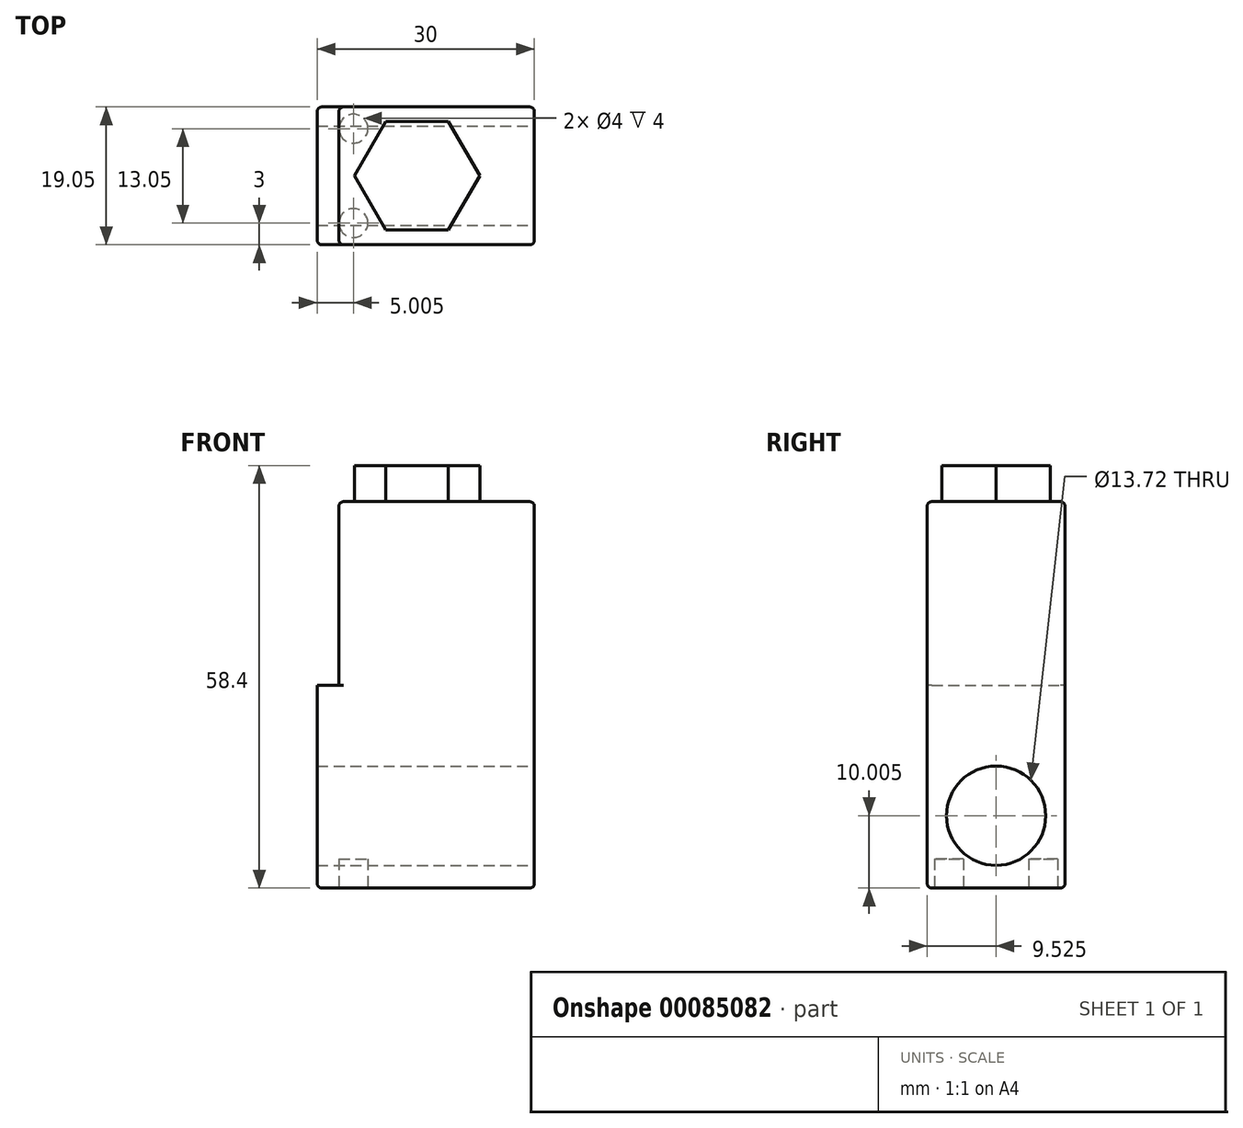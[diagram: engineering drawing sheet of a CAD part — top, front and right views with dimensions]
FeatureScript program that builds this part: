
annotation { "Feature Type Name" : "Feature", "Feature Type Description" : "" }
export const myFeature = defineFeature(function(context is Context, id is Id, definition is map)
    precondition{}
    {
        {
            var Q0;
            Q0=qCreatedBy(makeId("Front.planeOp"),FACE);
            var sketch = newSketch(context, id + "F0", { "sketchPlane" : qUnion([Q0])});
            skLineSegment(sketch, "E0.bottom", {"start": v(-15.44, -0.4) * mm, "end": v(14.56, -0.4) * mm});
            skLineSegment(sketch, "E0.top", {"start": v(-15.44, -28.4) * mm, "end": v(14.56, -28.4) * mm});
            skLineSegment(sketch, "E0.left", {"start": v(-15.44, -0.4) * mm, "end": v(-15.44, -28.4) * mm});
            skLineSegment(sketch, "E0.right", {"start": v(14.56, -0.4) * mm, "end": v(14.56, -28.4) * mm});
            skSolve(sketch);
        }
        {
            var Q0;
            Q0=qSketchRegion(id+"F0",true);
            var Q1;
            Q1=qSketchRegion(id+"F2",true);
            extrude(context, id + "F1", {"entities" : qUnion([Q0, Q1]), "depth" : 19.05 * mm});
        }
        {
            var Q0;
            Q0=makeQuery(id+"F1.opExtrude","SWEPT_FACE",FACE,{"disambiguationData":[OSD([sQuery(id+"F0.wireOp",EDGE,"E0.right")])]});
            var sketch = newSketch(context, id + "F2", { "sketchPlane" : qUnion([Q0])});
            skCircle(sketch, "E1", {"center": v(-9.53, -18.4) * mm, "radius": 6.86 * mm});
            skSolve(sketch);
        }
        {
            var Q0;
            Q0=qSketchRegion(id+"F2",true);
            extrude(context, id + "F3", {"entities" : qUnion([Q0]), "operationType" : NewBodyOperationType.REMOVE, "endBound" : BoundingType.THROUGH_ALL, "oppositeDirection" : true, "depth" : 25.4 * mm});
        }
        {
            var Q0;
            Q0=makeQuery(id+"F1.opExtrude","SWEPT_FACE",FACE,{"disambiguationData":[OSD([sQuery(id+"F0.wireOp",EDGE,"E0.bottom")])]});
            var sketch = newSketch(context, id + "F4", { "sketchPlane" : qUnion([Q0])});
            skLineSegment(sketch, "E2.0.0", {"start": v(13.93, 0) * mm, "end": v(-11.8, 0) * mm});
            skArc(sketch, "E2.0.1", {"start": v(-14.8, 0) * mm, "mid": v(-15.25, -0.19) * mm, "end": v(-15.44, -0.64) * mm});
            skLineSegment(sketch, "E2.0.2", {"start": v(-15.44, -0.64) * mm, "end": v(-15.44, -18.41) * mm});
            skArc(sketch, "E2.0.3", {"start": v(-15.44, -18.41) * mm, "mid": v(-15.25, -18.86) * mm, "end": v(-14.8, -19.05) * mm});
            skLineSegment(sketch, "E2.0.4", {"start": v(-14.8, -19.05) * mm, "end": v(13.93, -19.05) * mm});
            skArc(sketch, "E2.0.5", {"start": v(13.93, -19.05) * mm, "mid": v(14.38, -18.86) * mm, "end": v(14.56, -18.41) * mm});
            skLineSegment(sketch, "E2.0.6", {"start": v(14.56, -18.41) * mm, "end": v(14.56, -0.64) * mm});
            skArc(sketch, "E2.0.7", {"start": v(14.56, -0.64) * mm, "mid": v(14.38, -0.19) * mm, "end": v(13.93, 0) * mm});
            skLineSegment(sketch, "E3.bottom", {"start": v(-12.44, 0) * mm, "end": v(13.93, 0) * mm});
            skLineSegment(sketch, "E3.top", {"start": v(-11.8, -19.05) * mm, "end": v(13.93, -19.05) * mm});
            skLineSegment(sketch, "E3.left", {"start": v(-12.44, -0.64) * mm, "end": v(-12.44, -18.42) * mm});
            skLineSegment(sketch, "E3.right", {"start": v(14.56, -0.64) * mm, "end": v(14.56, -18.41) * mm});
            skPoint(sketch, "E4.newPointB", {"position": v(-14.8, 0) * mm});
            skArc(sketch, "E4.filletArc", {"start": v(-11.8, 0) * mm, "mid": v(-12.25, -0.19) * mm, "end": v(-12.44, -0.64) * mm});
            skPoint(sketch, "E5.visualSharp", {"position": v(-12.44, -19.05) * mm});
            skArc(sketch, "E5.filletArc", {"start": v(-12.44, -18.42) * mm, "mid": v(-12.25, -18.86) * mm, "end": v(-11.8, -19.05) * mm});
            skPoint(sketch, "E6.visualSharp", {"position": v(14.56, -19.05) * mm});
            skPoint(sketch, "E7.visualSharp", {"position": v(14.56, 0) * mm});
            skSolve(sketch);
        }
        {
            var Q0;
            Q0=qSketchRegion(id+"F4",true);
            extrude(context, id + "F5", {"entities" : qUnion([Q0]), "operationType" : NewBodyOperationType.ADD, "depth" : 25.4 * mm});
        }
        {
            var Q0;
            Q0=makeQuery(id+"F1.opExtrude","CAP_EDGE",EDGE,{"disambiguationData":[OSD([sQuery(id+"F0.wireOp",EDGE,"E0.right")])],"isStart":false});
            var Q1;
            Q1=makeQuery(id+"F1.opExtrude","CAP_EDGE",EDGE,{"disambiguationData":[OSD([sQuery(id+"F0.wireOp",EDGE,"E0.left")])],"isStart":false});
            var Q2;
            Q2=makeQuery(id+"F1.opExtrude","CAP_EDGE",EDGE,{"disambiguationData":[OSD([sQuery(id+"F0.wireOp",EDGE,"E0.right")])],"isStart":true});
            var Q3;
            Q3=makeQuery(id+"F1.opExtrude","CAP_EDGE",EDGE,{"disambiguationData":[OSD([sQuery(id+"F0.wireOp",EDGE,"E0.left")])],"isStart":true});
            var Q4;
            Q4=makeQuery(id+"F5.opExtrude","CAP_EDGE",EDGE,{"disambiguationData":[OSD([sQuery(id+"F4.wireOp",EDGE,"E3.bottom")])],"isStart":false});
            var Q5;
            Q5=makeQuery(id+"F5.opExtrude","CAP_EDGE",EDGE,{"disambiguationData":[OSD([sQuery(id+"F4.wireOp",EDGE,"E3.right")])],"isStart":false});
            var Q6;
            Q6=makeQuery(id+"F5.opExtrude","CAP_EDGE",EDGE,{"disambiguationData":[OSD([sQuery(id+"F4.wireOp",EDGE,"E3.top")])],"isStart":false});
            var Q7;
            Q7=makeQuery(id+"F5.opExtrude","CAP_EDGE",EDGE,{"disambiguationData":[OSD([sQuery(id+"F4.wireOp",EDGE,"E3.left")])],"isStart":false});
            var Q8;
            Q8=makeQuery(id+"F1.opExtrude","CAP_EDGE",EDGE,{"disambiguationData":[OSD([sQuery(id+"F0.wireOp",EDGE,"E0.top")])],"isStart":true});
            var Q9;
            Q9=makeQuery(id+"F1.opExtrude","SWEPT_EDGE",EDGE,{"disambiguationData":[OSD([sQuery(id+"F0.wireOp",EDGE,"E0.top"),sQuery(id+"F0.wireOp",EDGE,"E0.right")])]});
            var Q10;
            Q10=makeQuery(id+"F1.opExtrude","CAP_EDGE",EDGE,{"disambiguationData":[OSD([sQuery(id+"F0.wireOp",EDGE,"E0.top")])],"isStart":false});
            var Q11;
            Q11=makeQuery(id+"F1.opExtrude","SWEPT_EDGE",EDGE,{"disambiguationData":[OSD([sQuery(id+"F0.wireOp",EDGE,"E0.top"),sQuery(id+"F0.wireOp",EDGE,"E0.left")])]});
            fillet(context, id + "F6", {"entities" : qUnion([Q0, Q1, Q2, Q3, Q4, Q5, Q6, Q7, Q8, Q9, Q10, Q11]), "radius" : 0.64 * mm, "tangentPropagation" : true, "allowEdgeOverflow" : false});
        }
        {
            var Q0;
            Q0=makeQuery(id+"F1.opExtrude","SWEPT_FACE",FACE,{"disambiguationData":[OSD([sQuery(id+"F0.wireOp",EDGE,"E0.top")])]});
            var sketch = newSketch(context, id + "F7", { "sketchPlane" : qUnion([Q0])});
            skLineSegment(sketch, "E8.0.0", {"start": v(-14.8, 18.41) * mm, "end": v(-14.8, 0.64) * mm});
            skLineSegment(sketch, "E8.0.1", {"start": v(-14.8, 0.64) * mm, "end": v(13.93, 0.64) * mm});
            skLineSegment(sketch, "E8.0.2", {"start": v(13.93, 0.64) * mm, "end": v(13.93, 18.41) * mm});
            skLineSegment(sketch, "E8.0.3", {"start": v(13.93, 18.41) * mm, "end": v(-14.8, 18.41) * mm});
            skLineSegment(sketch, "E9.0.0", {"start": v(13.93, 18.41) * mm, "end": v(13.93, 19.05) * mm});
            skLineSegment(sketch, "E9.0.1", {"start": v(13.93, 19.05) * mm, "end": v(-14.8, 19.05) * mm});
            skLineSegment(sketch, "E9.0.2", {"start": v(-14.8, 19.05) * mm, "end": v(-14.8, 18.41) * mm});
            skLineSegment(sketch, "E10.0.0", {"start": v(-14.8, 18.41) * mm, "end": v(-14.8, 19.05) * mm});
            skArc(sketch, "E10.0.1", {"start": v(-14.8, 19.05) * mm, "mid": v(-15.25, 18.86) * mm, "end": v(-15.44, 18.41) * mm});
            skLineSegment(sketch, "E10.0.2", {"start": v(-14.8, 18.41) * mm, "end": v(-15.44, 18.41) * mm});
            skLineSegment(sketch, "E11.0.1", {"start": v(-15.44, 0.64) * mm, "end": v(-15.44, 18.41) * mm});
            skLineSegment(sketch, "E11.0.2", {"start": v(-15.44, 0.64) * mm, "end": v(-14.8, 0.64) * mm});
            skLineSegment(sketch, "E11.0.3", {"start": v(-14.8, 0.64) * mm, "end": v(-14.8, 18.41) * mm});
            skLineSegment(sketch, "E12.0.0", {"start": v(13.93, 0) * mm, "end": v(13.93, 0.64) * mm});
            skLineSegment(sketch, "E12.0.1", {"start": v(13.93, 0.64) * mm, "end": v(-14.8, 0.64) * mm});
            skLineSegment(sketch, "E12.0.2", {"start": v(-14.8, 0.64) * mm, "end": v(-14.8, 0) * mm});
            skLineSegment(sketch, "E12.0.3", {"start": v(13.93, 0) * mm, "end": v(-14.8, 0) * mm});
            skArc(sketch, "E13.0.0", {"start": v(-15.44, 0.64) * mm, "mid": v(-15.25, 0.19) * mm, "end": v(-14.8, 0) * mm});
            skLineSegment(sketch, "E13.0.1", {"start": v(-14.8, 0) * mm, "end": v(-14.8, 0.64) * mm});
            skArc(sketch, "E14.0.0", {"start": v(13.93, 0) * mm, "mid": v(14.38, 0.19) * mm, "end": v(14.56, 0.64) * mm});
            skLineSegment(sketch, "E14.0.1", {"start": v(14.56, 0.64) * mm, "end": v(13.93, 0.64) * mm});
            skLineSegment(sketch, "E15.0.0", {"start": v(13.93, 0.64) * mm, "end": v(14.56, 0.64) * mm});
            skLineSegment(sketch, "E15.0.1", {"start": v(14.56, 0.64) * mm, "end": v(14.56, 18.41) * mm});
            skLineSegment(sketch, "E15.0.2", {"start": v(14.56, 18.41) * mm, "end": v(13.93, 18.41) * mm});
            skLineSegment(sketch, "E16.0.0", {"start": v(13.93, 18.41) * mm, "end": v(14.56, 18.41) * mm});
            skArc(sketch, "E16.0.1", {"start": v(14.56, 18.41) * mm, "mid": v(14.38, 18.86) * mm, "end": v(13.93, 19.05) * mm});
            skCircle(sketch, "E17", {"center": v(-10.44, 16.05) * mm, "radius": 2 * mm});
            skCircle(sketch, "E18", {"center": v(-10.44, 3) * mm, "radius": 2 * mm});
            skSolve(sketch);
        }
        {
            var Q0;
            Q0=makeQuery(id+"F7.imprint","IMPRINT",FACE,{"disambiguationData":[TD([[makeQuery(id+"F7.imprint","IMPRINT",EDGE,{"derivedFrom":sQuery(id+"F7.wireOp",EDGE,"E17")}),1.0]])]});
            var Q1;
            Q1=makeQuery(id+"F7.imprint","IMPRINT",FACE,{"disambiguationData":[TD([[makeQuery(id+"F7.imprint","IMPRINT",EDGE,{"derivedFrom":sQuery(id+"F7.wireOp",EDGE,"E18")}),1.0]])]});
            extrude(context, id + "F8", {"entities" : qUnion([Q0, Q1]), "operationType" : NewBodyOperationType.REMOVE, "oppositeDirection" : true, "depth" : 4 * mm});
        }
        {
            var Q0;
            Q0=makeQuery(id+"F5.opExtrude","CAP_FACE",FACE,{"disambiguationData":[OSD([sQuery(id+"F4.wireOp",EDGE,"E3.bottom"),sQuery(id+"F4.wireOp",EDGE,"E3.top"),sQuery(id+"F4.wireOp",EDGE,"E3.left"),sQuery(id+"F4.wireOp",EDGE,"E3.right"),sQuery(id+"F4.wireOp",EDGE,"E4.filletArc"),sQuery(id+"F4.wireOp",EDGE,"E5.filletArc"),sQuery(id+"F4.wireOp",EDGE,"E2.0.5"),sQuery(id+"F4.wireOp",EDGE,"E2.0.7")])],"isStart":false});
            var sketch = newSketch(context, id + "F9", { "sketchPlane" : qUnion([Q0])});
            skLineSegment(sketch, "E19.0.0", {"start": v(-11.8, -18.41) * mm, "end": v(13.93, -18.41) * mm});
            skLineSegment(sketch, "E19.0.1", {"start": v(13.93, -18.41) * mm, "end": v(13.93, -0.64) * mm});
            skLineSegment(sketch, "E19.0.2", {"start": v(13.93, -0.64) * mm, "end": v(-11.8, -0.64) * mm});
            skLineSegment(sketch, "E19.0.3", {"start": v(-11.8, -0.64) * mm, "end": v(-11.8, -18.42) * mm});
            skCircle(sketch, "E20.cCircle", {"center": v(-1.64, -9.53) * mm, "radius": 7.5 * mm, "construction": true});
            skLineSegment(sketch, "E20.0", {"start": v(-5.97, -2.03) * mm, "end": v(2.69, -2.03) * mm});
            skLineSegment(sketch, "E20.1", {"start": v(2.69, -2.03) * mm, "end": v(7.02, -9.52) * mm});
            skLineSegment(sketch, "E20.2", {"start": v(7.02, -9.52) * mm, "end": v(2.69, -17.02) * mm});
            skLineSegment(sketch, "E20.3", {"start": v(2.69, -17.02) * mm, "end": v(-5.97, -17.02) * mm});
            skLineSegment(sketch, "E20.4", {"start": v(-5.97, -17.03) * mm, "end": v(-10.3, -9.52) * mm});
            skLineSegment(sketch, "E20.5", {"start": v(-10.3, -9.52) * mm, "end": v(-5.97, -2.03) * mm});
            skPoint(sketch, "E20.0.midPoint", {"position": v(-1.64, -2.03) * mm});
            skSolve(sketch);
        }
        {
            var Q0;
            Q0=makeQuery(id+"F9.imprint","IMPRINT",FACE,{"disambiguationData":[TD([[makeQuery(id+"F9.imprint","IMPRINT",EDGE,{"derivedFrom":sQuery(id+"F9.wireOp",EDGE,"E20.0")}),-1.0]])]});
            extrude(context, id + "F10", {"entities" : qUnion([Q0]), "operationType" : NewBodyOperationType.ADD, "depth" : 5 * mm});
        }
    });
